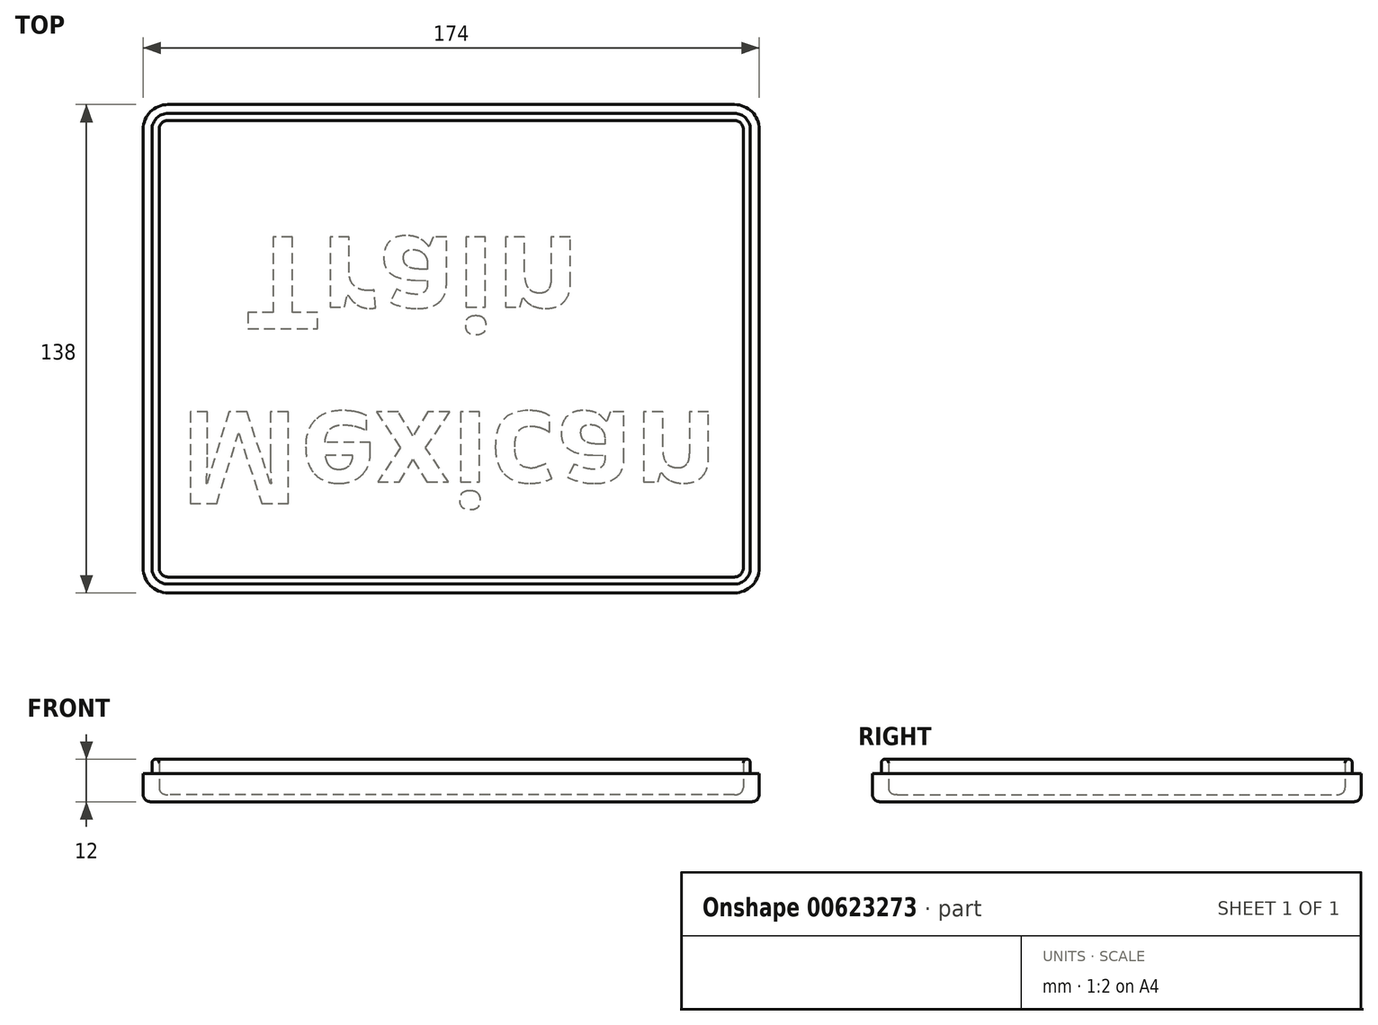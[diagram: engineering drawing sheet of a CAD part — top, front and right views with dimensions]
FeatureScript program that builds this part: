
annotation { "Feature Type Name" : "Feature", "Feature Type Description" : "" }
export const myFeature = defineFeature(function(context is Context, id is Id, definition is map)
    precondition{}
    {
        {
            var Q0;
            Q0=qCreatedBy(makeId("Top.planeOp"),FACE);
            var sketch = newSketch(context, id + "F0", { "sketchPlane" : qUnion([Q0])});
            skLineSegment(sketch, "E0.bottom", {"start": v(85, -67) * mm, "end": v(-85, -67) * mm});
            skLineSegment(sketch, "E0.top", {"start": v(85, 67) * mm, "end": v(-85, 67) * mm});
            skLineSegment(sketch, "E0.left", {"start": v(85, -67) * mm, "end": v(85, 67) * mm});
            skLineSegment(sketch, "E0.right", {"start": v(-85, -67) * mm, "end": v(-85, 67) * mm});
            skPoint(sketch, "E0.middle", {"position": v(0, 0) * mm});
            skLineSegment(sketch, "E1.bottom", {"start": v(87, -69) * mm, "end": v(-87, -69) * mm});
            skLineSegment(sketch, "E1.top", {"start": v(87, 69) * mm, "end": v(-87, 69) * mm});
            skLineSegment(sketch, "E1.left", {"start": v(87, -69) * mm, "end": v(87, 69) * mm});
            skLineSegment(sketch, "E1.right", {"start": v(-87, -69) * mm, "end": v(-87, 69) * mm});
            skLineSegment(sketch, "E2", {"start": v(-85, 49.12) * mm, "end": v(49, 49.12) * mm, "construction": true});
            skLineSegment(sketch, "E3", {"start": v(49, 49.12) * mm, "end": v(51, 49.12) * mm, "construction": true});
            skSolve(sketch);
        }
        {
            var Q0;
            Q0=makeQuery(id+"F0.imprint","IMPRINT",FACE,{"disambiguationData":[TD([[makeQuery(id+"F0.imprint","IMPRINT",EDGE,{"derivedFrom":sQuery(id+"F0.wireOp",EDGE,"E0.bottom")}),-1.0]])]});
            extrude(context, id + "F1", {"entities" : qUnion([Q0]), "depth" : 2 * mm, "offsetDistance" : 25 * mm});
        }
        {
            var Q0;
            Q0=makeQuery(id+"F0.imprint","IMPRINT",FACE,{"disambiguationData":[TD([[makeQuery(id+"F0.imprint","IMPRINT",EDGE,{"derivedFrom":sQuery(id+"F0.wireOp",EDGE,"E0.bottom")}),1.0]])]});
            extrude(context, id + "F2", {"entities" : qUnion([Q0]), "operationType" : NewBodyOperationType.ADD, "depth" : 2 * mm, "offsetDistance" : 25 * mm});
        }
        {
            var Q0;
            {var subQ0=sQuery(id+"F0.wireOp",EDGE,"E0.right");var subQ1=sQuery(id+"F0.wireOp",EDGE,"E0.left");var subQ2=sQuery(id+"F0.wireOp",EDGE,"E0.top");var subQ3=sQuery(id+"F0.wireOp",EDGE,"E0.bottom");Q0=makeQuery(id+"F2.boolean.opBoolean","MERGE",FACE,{"derivedFrom":[makeQuery(id+"F1.opExtrude","CAP_FACE",FACE,{"disambiguationData":[OSD([subQ3,subQ2,subQ1,subQ0])],"isStart":false}),makeQuery(id+"F2.opExtrude","CAP_FACE",FACE,{"disambiguationData":[OSD([subQ3,subQ2,subQ1,subQ0,sQuery(id+"F0.wireOp",EDGE,"E1.bottom"),sQuery(id+"F0.wireOp",EDGE,"E1.top"),sQuery(id+"F0.wireOp",EDGE,"E1.left"),sQuery(id+"F0.wireOp",EDGE,"E1.right")])],"isStart":false})]});}
            var sketch = newSketch(context, id + "F3", { "sketchPlane" : qUnion([Q0])});
            skLineSegment(sketch, "E4.bottom", {"start": v(84.5, -66.5) * mm, "end": v(-84.5, -66.5) * mm});
            skLineSegment(sketch, "E4.top", {"start": v(84.5, 66.5) * mm, "end": v(-84.5, 66.5) * mm});
            skLineSegment(sketch, "E4.left", {"start": v(84.5, -66.5) * mm, "end": v(84.5, 66.5) * mm});
            skLineSegment(sketch, "E4.right", {"start": v(-84.5, -66.5) * mm, "end": v(-84.5, 66.5) * mm});
            skPoint(sketch, "E4.middle", {"position": v(0, 0) * mm});
            skLineSegment(sketch, "E5.bottom", {"start": v(82.5, -64.5) * mm, "end": v(-82.5, -64.5) * mm});
            skLineSegment(sketch, "E5.top", {"start": v(82.5, 64.5) * mm, "end": v(-82.5, 64.5) * mm});
            skLineSegment(sketch, "E5.left", {"start": v(82.5, -64.5) * mm, "end": v(82.5, 64.5) * mm});
            skLineSegment(sketch, "E5.right", {"start": v(-82.5, -64.5) * mm, "end": v(-82.5, 64.5) * mm});
            skSolve(sketch);
        }
        {
            var Q0;
            Q0=makeQuery(id+"F3.imprint","IMPRINT",FACE,{"disambiguationData":[TD([[makeQuery(id+"F3.imprint","IMPRINT",EDGE,{"derivedFrom":sQuery(id+"F3.wireOp",EDGE,"E4.bottom")}),-1.0]])]});
            extrude(context, id + "F4", {"entities" : qUnion([Q0]), "operationType" : NewBodyOperationType.ADD, "depth" : 10 * mm, "offsetDistance" : 25 * mm});
        }
        {
            var Q0;
            Q0=makeQuery(id+"F4.opExtrude","SWEPT_EDGE",EDGE,{"disambiguationData":[OSD([sQuery(id+"F3.wireOp",EDGE,"E5.bottom"),sQuery(id+"F3.wireOp",EDGE,"E5.right")])]});
            var Q1;
            Q1=makeQuery(id+"F4.opExtrude","SWEPT_EDGE",EDGE,{"disambiguationData":[OSD([sQuery(id+"F3.wireOp",EDGE,"E5.top"),sQuery(id+"F3.wireOp",EDGE,"E5.right")])]});
            var Q2;
            Q2=makeQuery(id+"F4.opExtrude","SWEPT_EDGE",EDGE,{"disambiguationData":[OSD([sQuery(id+"F3.wireOp",EDGE,"E5.top"),sQuery(id+"F3.wireOp",EDGE,"E5.left")])]});
            var Q3;
            Q3=makeQuery(id+"F4.opExtrude","SWEPT_EDGE",EDGE,{"disambiguationData":[OSD([sQuery(id+"F3.wireOp",EDGE,"E5.bottom"),sQuery(id+"F3.wireOp",EDGE,"E5.left")])]});
            fillet(context, id + "F5", {"entities" : qUnion([Q0, Q1, Q2, Q3]), "radius" : 2.5 * mm, "tangentPropagation" : true, "allowEdgeOverflow" : false});
        }
        {
            var Q0;
            Q0=makeQuery(id+"F4.opExtrude","SWEPT_EDGE",EDGE,{"disambiguationData":[OSD([sQuery(id+"F3.wireOp",EDGE,"E4.top"),sQuery(id+"F3.wireOp",EDGE,"E4.right")])]});
            var Q1;
            Q1=makeQuery(id+"F4.opExtrude","SWEPT_EDGE",EDGE,{"disambiguationData":[OSD([sQuery(id+"F3.wireOp",EDGE,"E4.bottom"),sQuery(id+"F3.wireOp",EDGE,"E4.right")])]});
            var Q2;
            Q2=makeQuery(id+"F4.opExtrude","SWEPT_EDGE",EDGE,{"disambiguationData":[OSD([sQuery(id+"F3.wireOp",EDGE,"E4.bottom"),sQuery(id+"F3.wireOp",EDGE,"E4.left")])]});
            var Q3;
            Q3=makeQuery(id+"F4.opExtrude","SWEPT_EDGE",EDGE,{"disambiguationData":[OSD([sQuery(id+"F3.wireOp",EDGE,"E4.top"),sQuery(id+"F3.wireOp",EDGE,"E4.left")])]});
            fillet(context, id + "F6", {"entities" : qUnion([Q0, Q1, Q2, Q3]), "radius" : 4.5 * mm, "tangentPropagation" : true, "allowEdgeOverflow" : false});
        }
        {
            var Q0;
            Q0=makeQuery(id+"F2.opExtrude","SWEPT_EDGE",EDGE,{"disambiguationData":[OSD([sQuery(id+"F0.wireOp",EDGE,"E1.bottom"),sQuery(id+"F0.wireOp",EDGE,"E1.right")])]});
            var Q1;
            Q1=makeQuery(id+"F2.opExtrude","SWEPT_EDGE",EDGE,{"disambiguationData":[OSD([sQuery(id+"F0.wireOp",EDGE,"E1.bottom"),sQuery(id+"F0.wireOp",EDGE,"E1.left")])]});
            var Q2;
            Q2=makeQuery(id+"F2.opExtrude","SWEPT_EDGE",EDGE,{"disambiguationData":[OSD([sQuery(id+"F0.wireOp",EDGE,"E1.top"),sQuery(id+"F0.wireOp",EDGE,"E1.left")])]});
            var Q3;
            Q3=makeQuery(id+"F2.opExtrude","SWEPT_EDGE",EDGE,{"disambiguationData":[OSD([sQuery(id+"F0.wireOp",EDGE,"E1.top"),sQuery(id+"F0.wireOp",EDGE,"E1.right")])]});
            fillet(context, id + "F7", {"entities" : qUnion([Q0, Q1, Q2, Q3]), "radius" : 7 * mm, "tangentPropagation" : true, "allowEdgeOverflow" : false});
        }
        {
            var Q0;
            {var subQ0=sQuery(id+"F0.wireOp",EDGE,"E0.right");var subQ1=sQuery(id+"F0.wireOp",EDGE,"E0.left");var subQ2=sQuery(id+"F0.wireOp",EDGE,"E0.top");var subQ3=sQuery(id+"F0.wireOp",EDGE,"E0.bottom");Q0=makeQuery(id+"F2.boolean.opBoolean","MERGE",FACE,{"derivedFrom":[makeQuery(id+"F1.opExtrude","CAP_FACE",FACE,{"disambiguationData":[OSD([subQ3,subQ2,subQ1,subQ0])],"isStart":true}),makeQuery(id+"F2.opExtrude","CAP_FACE",FACE,{"disambiguationData":[OSD([subQ3,subQ2,subQ1,subQ0,sQuery(id+"F0.wireOp",EDGE,"E1.bottom"),sQuery(id+"F0.wireOp",EDGE,"E1.top"),sQuery(id+"F0.wireOp",EDGE,"E1.left"),sQuery(id+"F0.wireOp",EDGE,"E1.right")])],"isStart":true})]});}
            var sketch = newSketch(context, id + "F8", { "sketchPlane" : qUnion([Q0])});
            skLineSegment(sketch, "E6", {"start": v(-77, 69) * mm, "end": v(-77, -69) * mm, "construction": true});
            skLineSegment(sketch, "E7", {"start": v(-87, 44) * mm, "end": v(87, 44) * mm, "construction": true});
            skText(sketch, "E8", { "text": "Mexican\n  Train", "fontName": "OpenSans-Bold.ttf"});
            skLineSegment(sketch, "E9", {"start": v(-87, 56.62) * mm, "end": v(-77, 56.62) * mm, "construction": true});
            skLineSegment(sketch, "E10", {"start": v(-68.03, 69) * mm, "end": v(-68.03, 44) * mm, "construction": true});
            const initialGuessF8  = {"E8": [-0.077, 0.01783, 1, 0, 0.02617]};
            skSetInitialGuess(sketch, initialGuessF8);
            skSolve(sketch);
        }
        {
            var Q0;
            Q0=makeQuery(id+"F8.imprint","IMPRINT",FACE,{"disambiguationData":[TD([[makeQuery(id+"F8.imprint","IMPRINT",EDGE,{"derivedFrom":sQuery(id+"F8.wireOp",EDGE,"E8.sketch_text.stroke-0")}),-1.0]])]});
            var Q1;
            Q1=makeQuery(id+"F8.imprint","IMPRINT",FACE,{"disambiguationData":[TD([[makeQuery(id+"F8.imprint","IMPRINT",EDGE,{"derivedFrom":sQuery(id+"F8.wireOp",EDGE,"E8.sketch_text.stroke-19")}),-1.0]])]});
            var Q2;
            Q2=makeQuery(id+"F8.imprint","IMPRINT",FACE,{"disambiguationData":[TD([[makeQuery(id+"F8.imprint","IMPRINT",EDGE,{"derivedFrom":sQuery(id+"F8.wireOp",EDGE,"E8.sketch_text.stroke-39")}),-1.0]])]});
            var Q3;
            Q3=makeQuery(id+"F8.imprint","IMPRINT",FACE,{"disambiguationData":[TD([[makeQuery(id+"F8.imprint","IMPRINT",EDGE,{"derivedFrom":sQuery(id+"F8.wireOp",EDGE,"E8.sketch_text.stroke-56")}),-1.0]])]});
            var Q4;
            Q4=makeQuery(id+"F8.imprint","IMPRINT",FACE,{"disambiguationData":[TD([[makeQuery(id+"F8.imprint","IMPRINT",EDGE,{"derivedFrom":sQuery(id+"F8.wireOp",EDGE,"E8.sketch_text.stroke-51")}),-1.0]])]});
            var Q5;
            Q5=makeQuery(id+"F8.imprint","IMPRINT",FACE,{"disambiguationData":[TD([[makeQuery(id+"F8.imprint","IMPRINT",EDGE,{"derivedFrom":sQuery(id+"F8.wireOp",EDGE,"E8.sketch_text.stroke-60")}),-1.0]])]});
            var Q6;
            Q6=makeQuery(id+"F8.imprint","IMPRINT",FACE,{"disambiguationData":[TD([[makeQuery(id+"F8.imprint","IMPRINT",EDGE,{"derivedFrom":sQuery(id+"F8.wireOp",EDGE,"E8.sketch_text.stroke-74")}),-1.0]])]});
            var Q7;
            Q7=makeQuery(id+"F8.imprint","IMPRINT",FACE,{"disambiguationData":[TD([[makeQuery(id+"F8.imprint","IMPRINT",EDGE,{"derivedFrom":sQuery(id+"F8.wireOp",EDGE,"E8.sketch_text.stroke-99")}),-1.0]])]});
            var Q8;
            Q8=makeQuery(id+"F8.imprint","IMPRINT",FACE,{"disambiguationData":[TD([[makeQuery(id+"F8.imprint","IMPRINT",EDGE,{"derivedFrom":sQuery(id+"F8.wireOp",EDGE,"E8.sketch_text.stroke-116")}),-1.0]])]});
            var Q9;
            Q9=makeQuery(id+"F8.imprint","IMPRINT",FACE,{"disambiguationData":[TD([[makeQuery(id+"F8.imprint","IMPRINT",EDGE,{"derivedFrom":sQuery(id+"F8.wireOp",EDGE,"E8.sketch_text.stroke-124")}),-1.0]])]});
            var Q10;
            Q10=makeQuery(id+"F8.imprint","IMPRINT",FACE,{"disambiguationData":[TD([[makeQuery(id+"F8.imprint","IMPRINT",EDGE,{"derivedFrom":sQuery(id+"F8.wireOp",EDGE,"E8.sketch_text.stroke-137")}),-1.0]])]});
            var Q11;
            Q11=makeQuery(id+"F8.imprint","IMPRINT",FACE,{"disambiguationData":[TD([[makeQuery(id+"F8.imprint","IMPRINT",EDGE,{"derivedFrom":sQuery(id+"F8.wireOp",EDGE,"E8.sketch_text.stroke-167")}),-1.0]])]});
            var Q12;
            Q12=makeQuery(id+"F8.imprint","IMPRINT",FACE,{"disambiguationData":[TD([[makeQuery(id+"F8.imprint","IMPRINT",EDGE,{"derivedFrom":sQuery(id+"F8.wireOp",EDGE,"E8.sketch_text.stroke-162")}),-1.0]])]});
            var Q13;
            Q13=makeQuery(id+"F8.imprint","IMPRINT",FACE,{"disambiguationData":[TD([[makeQuery(id+"F8.imprint","IMPRINT",EDGE,{"derivedFrom":sQuery(id+"F8.wireOp",EDGE,"E8.sketch_text.stroke-171")}),-1.0]])]});
            extrude(context, id + "F9", {"entities" : qUnion([Q0, Q1, Q2, Q3, Q4, Q5, Q6, Q7, Q8, Q9, Q10, Q11, Q12, Q13]), "operationType" : NewBodyOperationType.REMOVE, "oppositeDirection" : true, "depth" : .1 * mm, "offsetDistance" : 25 * mm});
        }
        {
            var Q0;
            Q0=makeQuery(id+"F4.opExtrude","CAP_FACE",FACE,{"disambiguationData":[OSD([sQuery(id+"F3.wireOp",EDGE,"E4.bottom"),sQuery(id+"F3.wireOp",EDGE,"E4.top"),sQuery(id+"F3.wireOp",EDGE,"E4.left"),sQuery(id+"F3.wireOp",EDGE,"E4.right"),sQuery(id+"F3.wireOp",EDGE,"E5.bottom"),sQuery(id+"F3.wireOp",EDGE,"E5.top"),sQuery(id+"F3.wireOp",EDGE,"E5.left"),sQuery(id+"F3.wireOp",EDGE,"E5.right")])],"isStart":false});
            fillet(context, id + "F10", {"entities" : qUnion([Q0]), "radius" : 1 * mm, "tangentPropagation" : true, "allowEdgeOverflow" : false});
        }
        {
            var Q0;
            Q0=makeQuery(id+"F2.opExtrude","CAP_EDGE",EDGE,{"disambiguationData":[OSD([sQuery(id+"F0.wireOp",EDGE,"E1.bottom")])],"isStart":true});
            fillet(context, id + "F11", {"entities" : qUnion([Q0]), "radius" : 2 * mm, "tangentPropagation" : true, "allowEdgeOverflow" : false});
        }
        {
            var Q0;
            {var subQ0=sQuery(id+"F0.wireOp",EDGE,"E0.right");var subQ1=sQuery(id+"F0.wireOp",EDGE,"E0.left");var subQ2=sQuery(id+"F0.wireOp",EDGE,"E0.top");var subQ3=sQuery(id+"F0.wireOp",EDGE,"E0.bottom");Q0=makeQuery(id+"F4.boolean.opBoolean","SPLIT",FACE,{"disambiguationData":[TD([makeQuery(id+"F4.opExtrude","SWEPT_FACE",FACE,{"disambiguationData":[OSD([sQuery(id+"F3.wireOp",EDGE,"E5.bottom")])]})])],"derivedFrom":makeQuery(id+"F2.boolean.opBoolean","MERGE",FACE,{"derivedFrom":[makeQuery(id+"F1.opExtrude","CAP_FACE",FACE,{"disambiguationData":[OSD([subQ3,subQ2,subQ1,subQ0])],"isStart":false}),makeQuery(id+"F2.opExtrude","CAP_FACE",FACE,{"disambiguationData":[OSD([subQ3,subQ2,subQ1,subQ0,sQuery(id+"F0.wireOp",EDGE,"E1.bottom"),sQuery(id+"F0.wireOp",EDGE,"E1.top"),sQuery(id+"F0.wireOp",EDGE,"E1.left"),sQuery(id+"F0.wireOp",EDGE,"E1.right")])],"isStart":false})]})});}
            fillet(context, id + "F12", {"entities" : qUnion([Q0]), "radius" : 2 * mm, "tangentPropagation" : true, "allowEdgeOverflow" : false});
        }
        {
            var Q0;
            {var subQ0=sQuery(id+"F0.wireOp",EDGE,"E1.right");var subQ1=sQuery(id+"F0.wireOp",EDGE,"E1.left");var subQ2=sQuery(id+"F0.wireOp",EDGE,"E1.top");var subQ3=sQuery(id+"F0.wireOp",EDGE,"E1.bottom");var subQ4=sQuery(id+"F0.wireOp",EDGE,"E0.right");var subQ5=sQuery(id+"F0.wireOp",EDGE,"E0.left");var subQ6=sQuery(id+"F0.wireOp",EDGE,"E0.top");var subQ7=sQuery(id+"F0.wireOp",EDGE,"E0.bottom");Q0=makeQuery(id+"F4.boolean.opBoolean","SPLIT",FACE,{"disambiguationData":[TD([makeQuery(id+"F2.opExtrude","SWEPT_FACE",FACE,{"disambiguationData":[OSD([subQ3])]})])],"derivedFrom":makeQuery(id+"F2.boolean.opBoolean","MERGE",FACE,{"derivedFrom":[makeQuery(id+"F1.opExtrude","CAP_FACE",FACE,{"disambiguationData":[OSD([subQ7,subQ6,subQ5,subQ4])],"isStart":false}),makeQuery(id+"F2.opExtrude","CAP_FACE",FACE,{"disambiguationData":[OSD([subQ7,subQ6,subQ5,subQ4,subQ3,subQ2,subQ1,subQ0])],"isStart":false})]})});}
            extrude(context, id + "F13", {"entities" : qUnion([Q0]), "operationType" : NewBodyOperationType.ADD, "depth" : 6 * mm, "offsetDistance" : 25 * mm});
        }
    });
